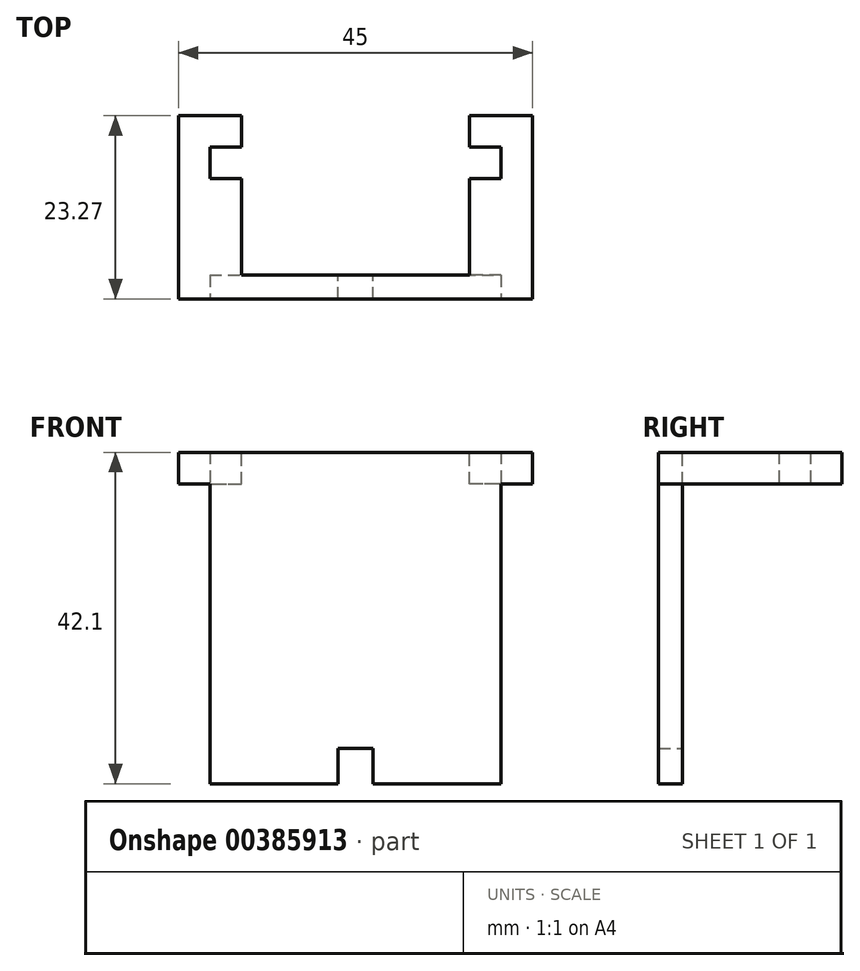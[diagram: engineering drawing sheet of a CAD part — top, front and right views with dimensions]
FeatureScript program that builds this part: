
annotation { "Feature Type Name" : "Feature", "Feature Type Description" : "" }
export const myFeature = defineFeature(function(context is Context, id is Id, definition is map)
    precondition{}
    {
        {
            var Q0;
            Q0=qCreatedBy(makeId("Front.planeOp"),FACE);
            var sketch = newSketch(context, id + "F0", { "sketchPlane" : qUnion([Q0])});
            skLineSegment(sketch, "E0.bottom", {"start": v(-18.5, 21.05) * mm, "end": v(18.5, 21.05) * mm});
            skLineSegment(sketch, "E0.top", {"start": v(-18.5, -21.05) * mm, "end": v(18.5, -21.05) * mm});
            skLineSegment(sketch, "E0.left", {"start": v(-18.5, 21.05) * mm, "end": v(-18.5, -21.05) * mm});
            skLineSegment(sketch, "E0.right", {"start": v(18.5, 21.05) * mm, "end": v(18.5, -21.05) * mm});
            skLineSegment(sketch, "E1.bottom", {"start": v(2.25, -21.05) * mm, "end": v(-2.25, -21.05) * mm});
            skLineSegment(sketch, "E1.top", {"start": v(2.25, -16.55) * mm, "end": v(-2.25, -16.55) * mm});
            skLineSegment(sketch, "E1.left", {"start": v(2.25, -21.05) * mm, "end": v(2.25, -16.55) * mm});
            skLineSegment(sketch, "E1.right", {"start": v(-2.25, -21.05) * mm, "end": v(-2.25, -16.55) * mm});
            skSolve(sketch);
        }
        {
            var Q0;
            Q0=makeQuery(id+"F0.imprint","IMPRINT",FACE,{"disambiguationData":[TD([[makeQuery(id+"F0.imprint","IMPRINT",EDGE,{"derivedFrom":sQuery(id+"F0.wireOp",EDGE,"E0.bottom")}),-1.0]])]});
            extrude(context, id + "F1", {"entities" : qUnion([Q0]), "depth" : 3 * mm});
        }
        {
            var Q0;
            Q0=qCreatedBy(makeId("Right.planeOp"),FACE);
            var sketch = newSketch(context, id + "F2", { "sketchPlane" : qUnion([Q0])});
            skLineSegment(sketch, "E2", {"start": v(0, 21.05) * mm, "end": v(12.27, 21.05) * mm});
            skLineSegment(sketch, "E3", {"start": v(12.27, 21.05) * mm, "end": v(12.27, 17.05) * mm});
            skLineSegment(sketch, "E4", {"start": v(12.27, 17.05) * mm, "end": v(0, 17.05) * mm});
            skLineSegment(sketch, "E5", {"start": v(0, 17.05) * mm, "end": v(0, 21.05) * mm});
            skSolve(sketch);
        }
        {
            var Q0;
            Q0 = qSketchRegion(id + "F2", true);
            extrude(context, id + "F3", {"entities" : qUnion([Q0]), "operationType" : NewBodyOperationType.ADD, "oppositeDirection" : true, "depth" : (37 / 2) * mm, "hasSecondDirection" : true, "secondDirectionOppositeDirection" : true, "secondDirectionDepth" : (18.5 - 4) * mm});
        }
        {
            var Q0;
            Q0=qCreatedBy(makeId("Top.planeOp"),FACE);
            var sketch = newSketch(context, id + "F4", { "sketchPlane" : qUnion([Q0])});
            skLineSegment(sketch, "E6", {"start": v(-18.5, -3) * mm, "end": v(-22.5, -3) * mm});
            skLineSegment(sketch, "E7", {"start": v(-22.5, -3) * mm, "end": v(-22.5, 20.27) * mm});
            skLineSegment(sketch, "E8", {"start": v(-22.5, 20.27) * mm, "end": v(-14.5, 20.27) * mm});
            skLineSegment(sketch, "E9", {"start": v(-14.5, 20.27) * mm, "end": v(-14.5, 16.27) * mm});
            skLineSegment(sketch, "E10", {"start": v(-14.5, 16.27) * mm, "end": v(-18.5, 16.27) * mm});
            skLineSegment(sketch, "E11", {"start": v(-18.5, 16.27) * mm, "end": v(-18.5, -3) * mm});
            skSolve(sketch);
        }
        {
            var Q0;
            Q0 = qSketchRegion(id + "F4", true);
            extrude(context, id + "F5", {"entities" : qUnion([Q0]), "operationType" : NewBodyOperationType.ADD, "depth" : (42.1 / 2) * mm, "hasSecondDirection" : true, "secondDirectionOppositeDirection" : false, "secondDirectionDepth" : (21.05 - 4) * mm});
        }
        {
            var Q0;
            Q0=makeQuery(id+"F1.opExtrude","SWEPT_BODY",BODY,{"disambiguationData":[OSD([sQuery(id+"F0.wireOp",EDGE,"E0.bottom"),sQuery(id+"F0.wireOp",EDGE,"E0.top"),sQuery(id+"F0.wireOp",EDGE,"E0.left"),sQuery(id+"F0.wireOp",EDGE,"E0.right"),sQuery(id+"F0.wireOp",EDGE,"E1.top"),sQuery(id+"F0.wireOp",EDGE,"E1.left"),sQuery(id+"F0.wireOp",EDGE,"E1.right")])]});
            var Q1;
            Q1=qCreatedBy(makeId("Right.planeOp"),FACE);
            mirror(context, id + "F6", {"operationType" : NewBodyOperationType.ADD, "entities" : qUnion([Q0]), "mirrorPlane" : qUnion([Q1])});
        }
    });
